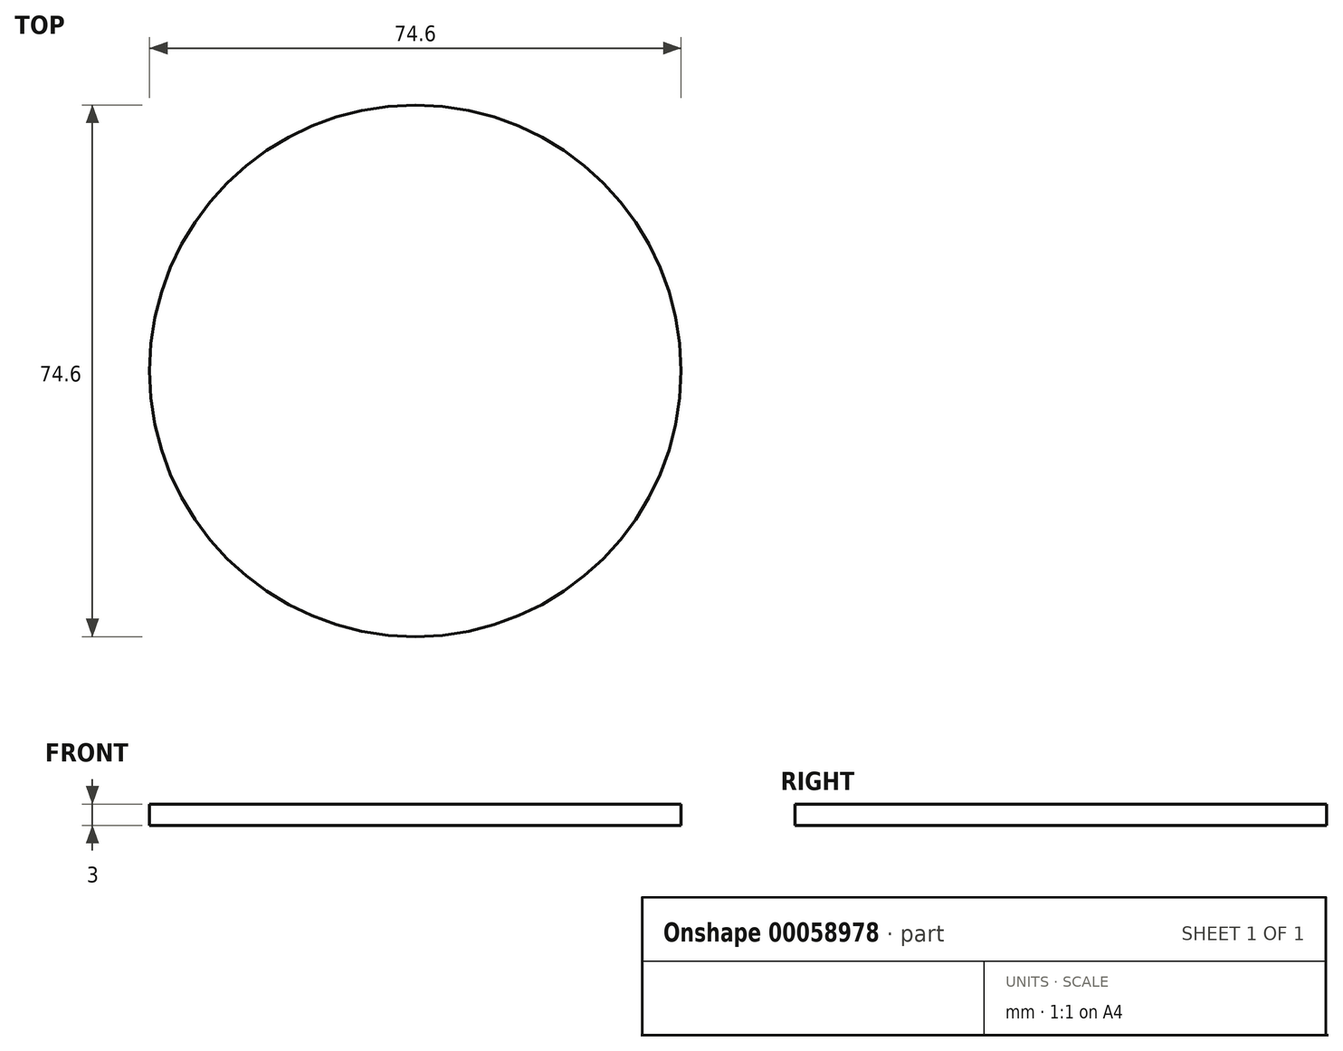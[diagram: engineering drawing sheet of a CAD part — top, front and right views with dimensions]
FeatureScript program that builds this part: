
annotation { "Feature Type Name" : "Feature", "Feature Type Description" : "" }
export const myFeature = defineFeature(function(context is Context, id is Id, definition is map)
    precondition{}
    {
        {
            var Q0;
            Q0=qCreatedBy(makeId("Top.planeOp"),FACE);
            var sketch = newSketch(context, id + "F0", { "sketchPlane" : qUnion([Q0])});
            skCircle(sketch, "E0", {"center": v(0, 0) * mm, "radius": 37.3 * mm});
            skSolve(sketch);
        }
        {
            var Q0;
            Q0=qSketchRegion(id+"F0",true);
            extrude(context, id + "F1", {"entities" : qUnion([Q0]), "depth" : 3 * mm});
        }
    });
